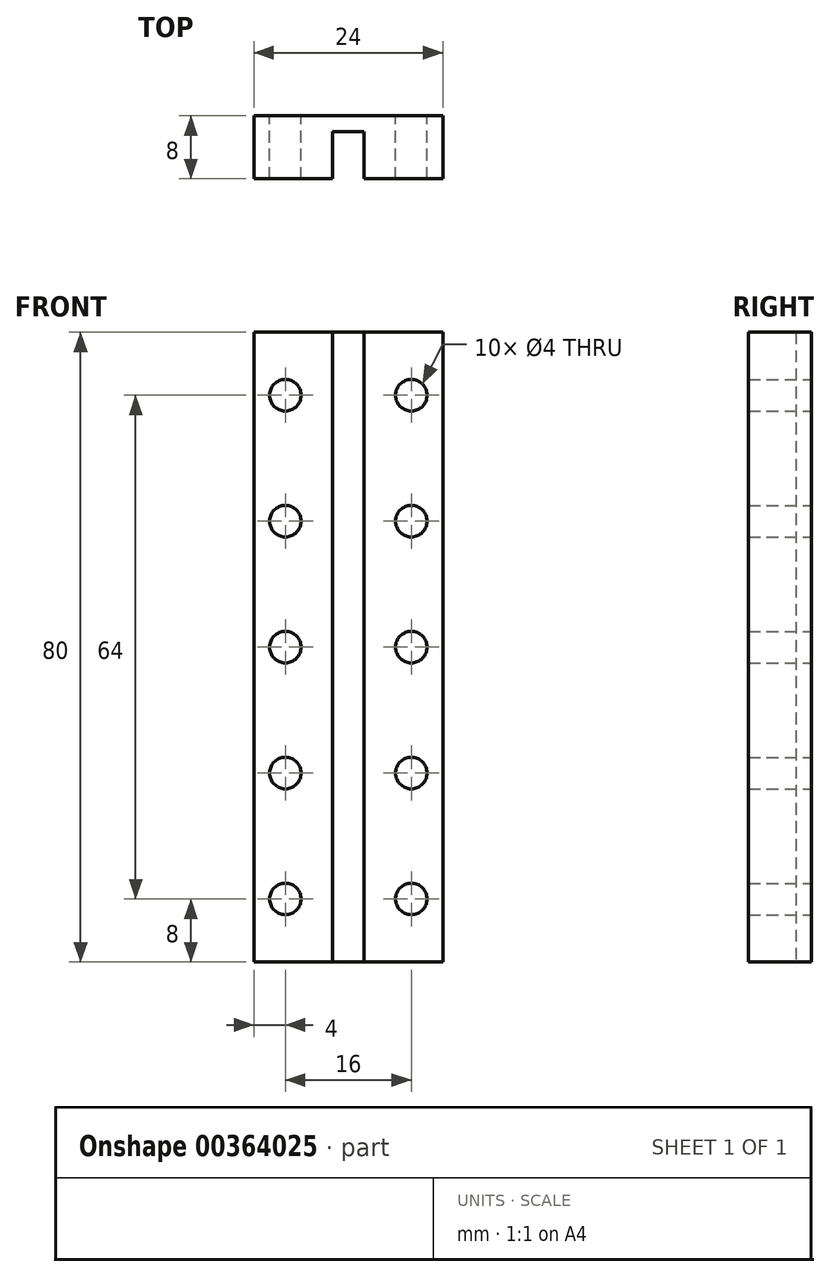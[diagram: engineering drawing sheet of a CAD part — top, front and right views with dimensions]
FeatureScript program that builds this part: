
annotation { "Feature Type Name" : "Feature", "Feature Type Description" : "" }
export const myFeature = defineFeature(function(context is Context, id is Id, definition is map)
    precondition{}
    {
        {
            var Q0;
            Q0=qCreatedBy(makeId("Top.planeOp"),FACE);
            var sketch = newSketch(context, id + "F0", { "sketchPlane" : qUnion([Q0])});
            skLineSegment(sketch, "E0.top", {"start": v(12, 4) * mm, "end": v(-12, 4) * mm});
            skLineSegment(sketch, "E0.left", {"start": v(12, -4) * mm, "end": v(12, 4) * mm});
            skLineSegment(sketch, "E0.right", {"start": v(-12, -4) * mm, "end": v(-12, 4) * mm});
            skPoint(sketch, "E0.middle", {"position": v(0, 0) * mm});
            skLineSegment(sketch, "E1", {"start": v(-12, -4) * mm, "end": v(-2, -4) * mm});
            skLineSegment(sketch, "E2", {"start": v(-2, -4) * mm, "end": v(-2, 2) * mm});
            skLineSegment(sketch, "E3", {"start": v(-2, 2) * mm, "end": v(2, 2) * mm});
            skLineSegment(sketch, "E4", {"start": v(2, 2) * mm, "end": v(2, -4) * mm});
            skLineSegment(sketch, "E5", {"start": v(2, -4) * mm, "end": v(12, -4) * mm});
            skSolve(sketch);
        }
        {
            var Q0;
            Q0=qSketchRegion(id+"F0",true);
            extrude(context, id + "F1", {"entities" : qUnion([Q0]), "depth" : 80 * mm});
        }
        {
            var Q0;
            Q0=makeQuery(id+"F1.opExtrude","SWEPT_FACE",FACE,{"disambiguationData":[OSD([sQuery(id+"F0.wireOp",EDGE,"E0.top")])]});
            var sketch = newSketch(context, id + "F2", { "sketchPlane" : qUnion([Q0])});
            skLineSegment(sketch, "E6", {"start": v(-8, 0) * mm, "end": v(-8, 8) * mm, "construction": true});
            skCircle(sketch, "E7", {"center": v(-8, 8) * mm, "radius": 2 * mm});
            skCircle(sketch, "E8.0.1.0", {"center": v(-8, 24) * mm, "radius": 2 * mm});
            skCircle(sketch, "E8.0.2.0", {"center": v(-8, 40) * mm, "radius": 2 * mm});
            skCircle(sketch, "E8.0.3.0", {"center": v(-8, 56) * mm, "radius": 2 * mm});
            skCircle(sketch, "E8.0.4.0", {"center": v(-8, 72) * mm, "radius": 2 * mm});
            skCircle(sketch, "E8.1.0.0", {"center": v(8, 8) * mm, "radius": 2 * mm});
            skCircle(sketch, "E8.1.1.0", {"center": v(8, 24) * mm, "radius": 2 * mm});
            skCircle(sketch, "E8.1.2.0", {"center": v(8, 40) * mm, "radius": 2 * mm});
            skCircle(sketch, "E8.1.3.0", {"center": v(8, 56) * mm, "radius": 2 * mm});
            skCircle(sketch, "E8.1.4.0", {"center": v(8, 72) * mm, "radius": 2 * mm});
            skLineSegment(sketch, "E8.direction1", {"start": v(-8, 8) * mm, "end": v(8, 8) * mm, "construction": true});
            skLineSegment(sketch, "E8.direction2", {"start": v(-8, 8) * mm, "end": v(-8, 24) * mm, "construction": true});
            skCircle(sketch, "E9.0.0.5", {"center": v(-8, 88) * mm, "radius": 2 * mm});
            skCircle(sketch, "E9.0.0.6", {"center": v(-8, 104) * mm, "radius": 2 * mm});
            skCircle(sketch, "E9.0.0.7", {"center": v(-8, 120) * mm, "radius": 2 * mm});
            skCircle(sketch, "E9.0.0.8", {"center": v(-8, 136) * mm, "radius": 2 * mm});
            skCircle(sketch, "E9.0.0.9", {"center": v(-8, 152) * mm, "radius": 2 * mm});
            skCircle(sketch, "E9.0.1.5", {"center": v(8, 88) * mm, "radius": 2 * mm});
            skCircle(sketch, "E9.0.1.6", {"center": v(8, 104) * mm, "radius": 2 * mm});
            skCircle(sketch, "E9.0.1.7", {"center": v(8, 120) * mm, "radius": 2 * mm});
            skCircle(sketch, "E9.0.1.8", {"center": v(8, 136) * mm, "radius": 2 * mm});
            skCircle(sketch, "E9.0.1.9", {"center": v(8, 152) * mm, "radius": 2 * mm});
            skSolve(sketch);
        }
        {
            var Q0;
            Q0=qSketchRegion(id+"F2",true);
            extrude(context, id + "F3", {"entities" : qUnion([Q0]), "operationType" : NewBodyOperationType.REMOVE, "oppositeDirection" : true, "depth" : 25 * mm});
        }
    });
